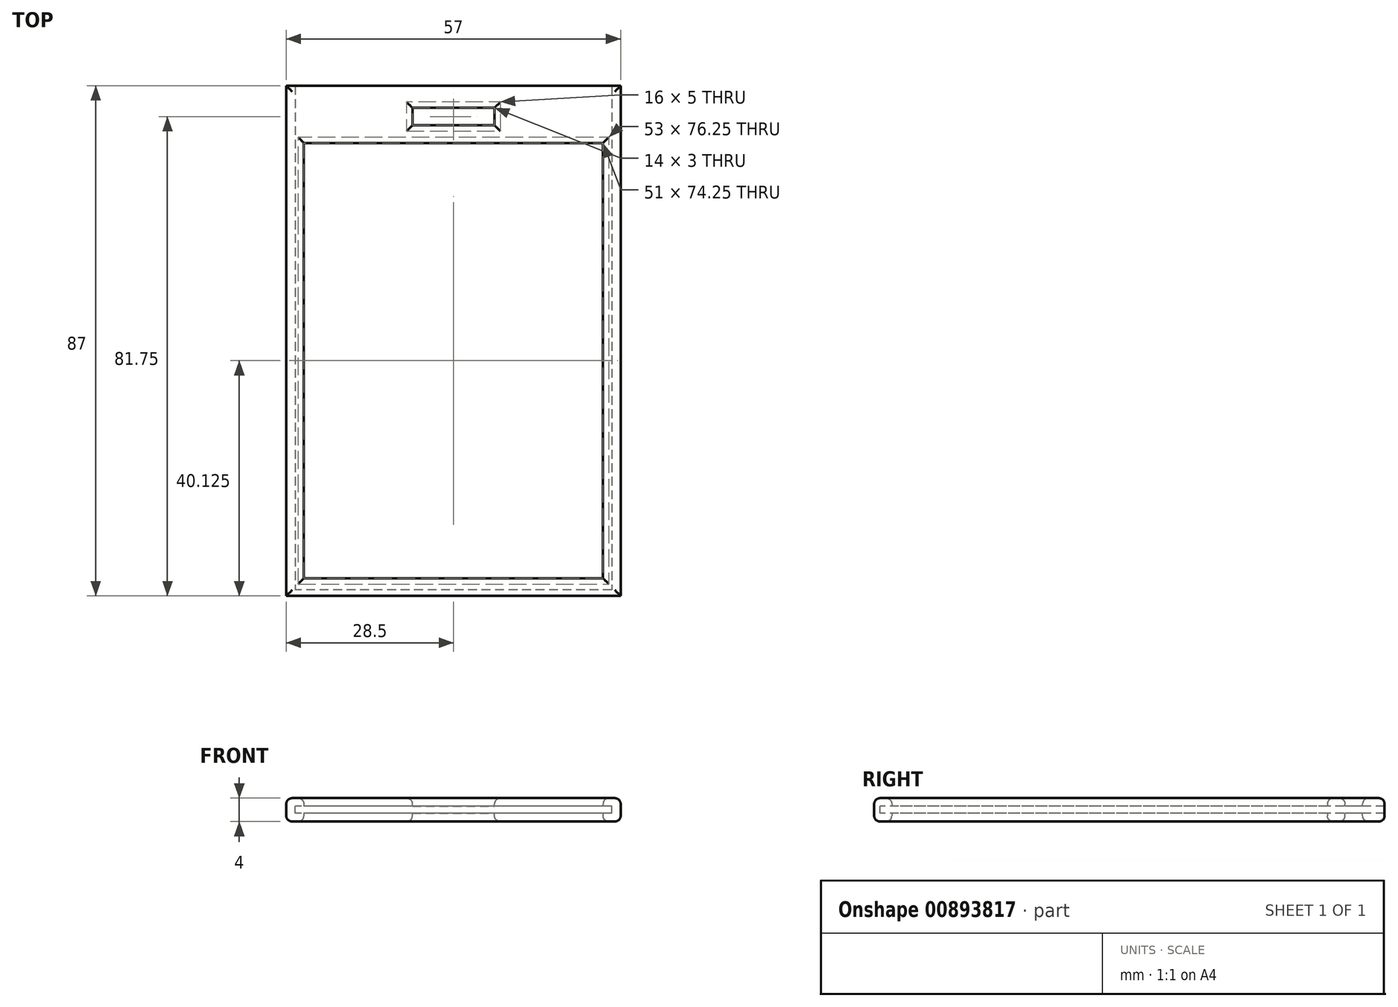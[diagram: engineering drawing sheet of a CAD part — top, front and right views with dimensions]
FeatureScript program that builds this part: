
annotation { "Feature Type Name" : "Feature", "Feature Type Description" : "" }
export const myFeature = defineFeature(function(context is Context, id is Id, definition is map)
    precondition{}
    {
        {
            var Q0;
            Q0=qCreatedBy(makeId("Top.planeOp"),FACE);
            var sketch = newSketch(context, id + "F0", { "sketchPlane" : qUnion([Q0])});
            skLineSegment(sketch, "E0.bottom", {"start": v(28.5, -43.5) * mm, "end": v(-28.5, -43.5) * mm});
            skLineSegment(sketch, "E0.top", {"start": v(28.5, 43.5) * mm, "end": v(-28.5, 43.5) * mm});
            skLineSegment(sketch, "E0.left", {"start": v(28.5, -43.5) * mm, "end": v(28.5, 43.5) * mm});
            skLineSegment(sketch, "E0.right", {"start": v(-28.5, -43.5) * mm, "end": v(-28.5, 43.5) * mm});
            skPoint(sketch, "E0.middle", {"position": v(0, 0) * mm});
            skSolve(sketch);
        }
        {
            var Q0;
            Q0 = qSketchRegion(id + "F0", true);
            extrude(context, id + "F1", {"entities" : qUnion([Q0]), "endBound" : BoundingType.SYMMETRIC, "depth" : 4 * mm, "offsetDistance" : 25 * mm});
        }
        {
            var Q0;
            Q0=qCreatedBy(makeId("Top.planeOp"),FACE);
            var sketch = newSketch(context, id + "F2", { "sketchPlane" : qUnion([Q0])});
            skLineSegment(sketch, "E1.bottom", {"start": v(7, 36.75) * mm, "end": v(-7, 36.75) * mm});
            skLineSegment(sketch, "E1.top", {"start": v(7, 39.75) * mm, "end": v(-7, 39.75) * mm});
            skLineSegment(sketch, "E1.left", {"start": v(7, 36.75) * mm, "end": v(7, 39.75) * mm});
            skLineSegment(sketch, "E1.right", {"start": v(-7, 36.75) * mm, "end": v(-7, 39.75) * mm});
            skPoint(sketch, "E1.middle", {"position": v(0, 38.25) * mm});
            skSolve(sketch);
        }
        {
            var Q0;
            Q0 = qSketchRegion(id + "F2", true);
            extrude(context, id + "F3", {"entities" : qUnion([Q0]), "operationType" : NewBodyOperationType.REMOVE, "endBound" : BoundingType.SYMMETRIC, "oppositeDirection" : true, "depth" : 25 * mm, "offsetDistance" : 25 * mm});
        }
        {
            var Q0;
            Q0=qCreatedBy(makeId("Front.planeOp"),FACE);
            var sketch = newSketch(context, id + "F4", { "sketchPlane" : qUnion([Q0])});
            skLineSegment(sketch, "E2.bottom", {"start": v(27, -0.6) * mm, "end": v(-27, -0.6) * mm});
            skLineSegment(sketch, "E2.top", {"start": v(27, 0.6) * mm, "end": v(-27, 0.6) * mm});
            skLineSegment(sketch, "E2.left", {"start": v(27, -0.6) * mm, "end": v(27, 0.6) * mm});
            skLineSegment(sketch, "E2.right", {"start": v(-27, -0.6) * mm, "end": v(-27, 0.6) * mm});
            skPoint(sketch, "E2.middle", {"position": v(0, 0) * mm});
            skSolve(sketch);
        }
        {
            var Q0;
            Q0 = qSketchRegion(id + "F4", true);
            extrude(context, id + "F5", {"entities" : qUnion([Q0]), "operationType" : NewBodyOperationType.REMOVE, "oppositeDirection" : true, "depth" : 50 * mm, "offsetDistance" : 25 * mm, "hasSecondDirection" : true, "secondDirectionOppositeDirection" : false, "secondDirectionDepth" : 42.5 * mm});
        }
        {
            var Q0;
            Q0=qCreatedBy(makeId("Top.planeOp"),FACE);
            var sketch = newSketch(context, id + "F6", { "sketchPlane" : qUnion([Q0])});
            skLineSegment(sketch, "E3.bottom", {"start": v(0, 0) * mm, "end": v(25.5, 0) * mm});
            skLineSegment(sketch, "E3.top", {"start": v(0, 33.75) * mm, "end": v(25.5, 33.75) * mm});
            skLineSegment(sketch, "E3.left", {"start": v(0, 0) * mm, "end": v(0, 33.75) * mm});
            skLineSegment(sketch, "E3.right", {"start": v(25.5, 0) * mm, "end": v(25.5, 33.75) * mm});
            skLineSegment(sketch, "E4.top", {"start": v(0, -40.5) * mm, "end": v(25.5, -40.5) * mm});
            skLineSegment(sketch, "E4.left", {"start": v(0, 0) * mm, "end": v(0, -40.5) * mm});
            skLineSegment(sketch, "E4.right", {"start": v(25.5, 0) * mm, "end": v(25.5, -40.5) * mm});
            skLineSegment(sketch, "E5.bottom", {"start": v(0, 0) * mm, "end": v(-25.5, 0) * mm});
            skLineSegment(sketch, "E5.top", {"start": v(0, -40.5) * mm, "end": v(-25.5, -40.5) * mm});
            skLineSegment(sketch, "E5.right", {"start": v(-25.5, 0) * mm, "end": v(-25.5, -40.5) * mm});
            skLineSegment(sketch, "E6.top", {"start": v(0, 33.75) * mm, "end": v(-25.5, 33.75) * mm});
            skLineSegment(sketch, "E6.right", {"start": v(-25.5, 0) * mm, "end": v(-25.5, 33.75) * mm});
            skSolve(sketch);
        }
        {
            var Q0;
            Q0 = qSketchRegion(id + "F6", true);
            extrude(context, id + "F7", {"entities" : qUnion([Q0]), "operationType" : NewBodyOperationType.REMOVE, "endBound" : BoundingType.SYMMETRIC, "depth" : 25 * mm, "offsetDistance" : 25 * mm});
        }
        {
            var Q0;
            Q0=makeQuery(id+"F1.opExtrude","CAP_EDGE",EDGE,{"disambiguationData":[OSD([sQuery(id+"F0.wireOp",EDGE,"E0.right")])],"isStart":false});
            var Q1;
            Q1=makeQuery(id+"F7.boolean.opBoolean","INTERSECT",EDGE,{"derivedFrom":[makeQuery(id+"F1.opExtrude","CAP_FACE",FACE,{"disambiguationData":[OSD([sQuery(id+"F0.wireOp",EDGE,"E0.bottom"),sQuery(id+"F0.wireOp",EDGE,"E0.top"),sQuery(id+"F0.wireOp",EDGE,"E0.left"),sQuery(id+"F0.wireOp",EDGE,"E0.right")])],"isStart":false}),makeQuery(id+"F7.opExtrude","SWEPT_FACE",FACE,{"disambiguationData":[OSD([sQuery(id+"F6.wireOp",EDGE,"E5.right"),sQuery(id+"F6.wireOp",EDGE,"E6.right")])]})]});
            var Q2;
            Q2=makeQuery(id+"F7.boolean.opBoolean","INTERSECT",EDGE,{"derivedFrom":[makeQuery(id+"F1.opExtrude","CAP_FACE",FACE,{"disambiguationData":[OSD([sQuery(id+"F0.wireOp",EDGE,"E0.bottom"),sQuery(id+"F0.wireOp",EDGE,"E0.top"),sQuery(id+"F0.wireOp",EDGE,"E0.left"),sQuery(id+"F0.wireOp",EDGE,"E0.right")])],"isStart":false}),makeQuery(id+"F7.opExtrude","SWEPT_FACE",FACE,{"disambiguationData":[OSD([sQuery(id+"F6.wireOp",EDGE,"E4.top"),sQuery(id+"F6.wireOp",EDGE,"E5.top")])]})]});
            var Q3;
            Q3=makeQuery(id+"F1.opExtrude","CAP_EDGE",EDGE,{"disambiguationData":[OSD([sQuery(id+"F0.wireOp",EDGE,"E0.bottom")])],"isStart":false});
            var Q4;
            Q4=makeQuery(id+"F7.boolean.opBoolean","INTERSECT",EDGE,{"derivedFrom":[makeQuery(id+"F1.opExtrude","CAP_FACE",FACE,{"disambiguationData":[OSD([sQuery(id+"F0.wireOp",EDGE,"E0.bottom"),sQuery(id+"F0.wireOp",EDGE,"E0.top"),sQuery(id+"F0.wireOp",EDGE,"E0.left"),sQuery(id+"F0.wireOp",EDGE,"E0.right")])],"isStart":false}),makeQuery(id+"F7.opExtrude","SWEPT_FACE",FACE,{"disambiguationData":[OSD([sQuery(id+"F6.wireOp",EDGE,"E3.right"),sQuery(id+"F6.wireOp",EDGE,"E4.right")])]})]});
            var Q5;
            Q5=makeQuery(id+"F1.opExtrude","CAP_EDGE",EDGE,{"disambiguationData":[OSD([sQuery(id+"F0.wireOp",EDGE,"E0.left")])],"isStart":false});
            var Q6;
            Q6=makeQuery(id+"F7.boolean.opBoolean","INTERSECT",EDGE,{"derivedFrom":[makeQuery(id+"F1.opExtrude","CAP_FACE",FACE,{"disambiguationData":[OSD([sQuery(id+"F0.wireOp",EDGE,"E0.bottom"),sQuery(id+"F0.wireOp",EDGE,"E0.top"),sQuery(id+"F0.wireOp",EDGE,"E0.left"),sQuery(id+"F0.wireOp",EDGE,"E0.right")])],"isStart":false}),makeQuery(id+"F7.opExtrude","SWEPT_FACE",FACE,{"disambiguationData":[OSD([sQuery(id+"F6.wireOp",EDGE,"E3.top"),sQuery(id+"F6.wireOp",EDGE,"E6.top")])]})]});
            var Q7;
            Q7=makeQuery(id+"F1.opExtrude","CAP_EDGE",EDGE,{"disambiguationData":[OSD([sQuery(id+"F0.wireOp",EDGE,"E0.top")])],"isStart":false});
            var Q8;
            Q8=makeQuery(id+"F1.opExtrude","CAP_EDGE",EDGE,{"disambiguationData":[OSD([sQuery(id+"F0.wireOp",EDGE,"E0.right")])],"isStart":true});
            var Q9;
            Q9=makeQuery(id+"F1.opExtrude","CAP_EDGE",EDGE,{"disambiguationData":[OSD([sQuery(id+"F0.wireOp",EDGE,"E0.top")])],"isStart":true});
            var Q10;
            Q10=makeQuery(id+"F7.boolean.opBoolean","INTERSECT",EDGE,{"derivedFrom":[makeQuery(id+"F1.opExtrude","CAP_FACE",FACE,{"disambiguationData":[OSD([sQuery(id+"F0.wireOp",EDGE,"E0.bottom"),sQuery(id+"F0.wireOp",EDGE,"E0.top"),sQuery(id+"F0.wireOp",EDGE,"E0.left"),sQuery(id+"F0.wireOp",EDGE,"E0.right")])],"isStart":true}),makeQuery(id+"F7.opExtrude","SWEPT_FACE",FACE,{"disambiguationData":[OSD([sQuery(id+"F6.wireOp",EDGE,"E3.top"),sQuery(id+"F6.wireOp",EDGE,"E6.top")])]})]});
            var Q11;
            Q11=makeQuery(id+"F7.boolean.opBoolean","INTERSECT",EDGE,{"derivedFrom":[makeQuery(id+"F1.opExtrude","CAP_FACE",FACE,{"disambiguationData":[OSD([sQuery(id+"F0.wireOp",EDGE,"E0.bottom"),sQuery(id+"F0.wireOp",EDGE,"E0.top"),sQuery(id+"F0.wireOp",EDGE,"E0.left"),sQuery(id+"F0.wireOp",EDGE,"E0.right")])],"isStart":true}),makeQuery(id+"F7.opExtrude","SWEPT_FACE",FACE,{"disambiguationData":[OSD([sQuery(id+"F6.wireOp",EDGE,"E3.right"),sQuery(id+"F6.wireOp",EDGE,"E4.right")])]})]});
            var Q12;
            Q12=makeQuery(id+"F7.boolean.opBoolean","INTERSECT",EDGE,{"derivedFrom":[makeQuery(id+"F1.opExtrude","CAP_FACE",FACE,{"disambiguationData":[OSD([sQuery(id+"F0.wireOp",EDGE,"E0.bottom"),sQuery(id+"F0.wireOp",EDGE,"E0.top"),sQuery(id+"F0.wireOp",EDGE,"E0.left"),sQuery(id+"F0.wireOp",EDGE,"E0.right")])],"isStart":true}),makeQuery(id+"F7.opExtrude","SWEPT_FACE",FACE,{"disambiguationData":[OSD([sQuery(id+"F6.wireOp",EDGE,"E5.right"),sQuery(id+"F6.wireOp",EDGE,"E6.right")])]})]});
            var Q13;
            Q13=makeQuery(id+"F1.opExtrude","CAP_EDGE",EDGE,{"disambiguationData":[OSD([sQuery(id+"F0.wireOp",EDGE,"E0.left")])],"isStart":true});
            var Q14;
            Q14=makeQuery(id+"F7.boolean.opBoolean","INTERSECT",EDGE,{"derivedFrom":[makeQuery(id+"F1.opExtrude","CAP_FACE",FACE,{"disambiguationData":[OSD([sQuery(id+"F0.wireOp",EDGE,"E0.bottom"),sQuery(id+"F0.wireOp",EDGE,"E0.top"),sQuery(id+"F0.wireOp",EDGE,"E0.left"),sQuery(id+"F0.wireOp",EDGE,"E0.right")])],"isStart":true}),makeQuery(id+"F7.opExtrude","SWEPT_FACE",FACE,{"disambiguationData":[OSD([sQuery(id+"F6.wireOp",EDGE,"E4.top"),sQuery(id+"F6.wireOp",EDGE,"E5.top")])]})]});
            var Q15;
            Q15=makeQuery(id+"F3.boolean.opBoolean","INTERSECT",EDGE,{"derivedFrom":[makeQuery(id+"F1.opExtrude","CAP_FACE",FACE,{"disambiguationData":[OSD([sQuery(id+"F0.wireOp",EDGE,"E0.bottom"),sQuery(id+"F0.wireOp",EDGE,"E0.top"),sQuery(id+"F0.wireOp",EDGE,"E0.left"),sQuery(id+"F0.wireOp",EDGE,"E0.right")])],"isStart":true}),makeQuery(id+"F3.opExtrude","SWEPT_FACE",FACE,{"disambiguationData":[OSD([sQuery(id+"F2.wireOp",EDGE,"E1.bottom")])]})]});
            var Q16;
            Q16=makeQuery(id+"F3.boolean.opBoolean","INTERSECT",EDGE,{"derivedFrom":[makeQuery(id+"F1.opExtrude","CAP_FACE",FACE,{"disambiguationData":[OSD([sQuery(id+"F0.wireOp",EDGE,"E0.bottom"),sQuery(id+"F0.wireOp",EDGE,"E0.top"),sQuery(id+"F0.wireOp",EDGE,"E0.left"),sQuery(id+"F0.wireOp",EDGE,"E0.right")])],"isStart":true}),makeQuery(id+"F3.opExtrude","SWEPT_FACE",FACE,{"disambiguationData":[OSD([sQuery(id+"F2.wireOp",EDGE,"E1.left")])]})]});
            var Q17;
            Q17=makeQuery(id+"F3.boolean.opBoolean","INTERSECT",EDGE,{"derivedFrom":[makeQuery(id+"F1.opExtrude","CAP_FACE",FACE,{"disambiguationData":[OSD([sQuery(id+"F0.wireOp",EDGE,"E0.bottom"),sQuery(id+"F0.wireOp",EDGE,"E0.top"),sQuery(id+"F0.wireOp",EDGE,"E0.left"),sQuery(id+"F0.wireOp",EDGE,"E0.right")])],"isStart":true}),makeQuery(id+"F3.opExtrude","SWEPT_FACE",FACE,{"disambiguationData":[OSD([sQuery(id+"F2.wireOp",EDGE,"E1.right")])]})]});
            var Q18;
            Q18=makeQuery(id+"F3.boolean.opBoolean","INTERSECT",EDGE,{"derivedFrom":[makeQuery(id+"F1.opExtrude","CAP_FACE",FACE,{"disambiguationData":[OSD([sQuery(id+"F0.wireOp",EDGE,"E0.bottom"),sQuery(id+"F0.wireOp",EDGE,"E0.top"),sQuery(id+"F0.wireOp",EDGE,"E0.left"),sQuery(id+"F0.wireOp",EDGE,"E0.right")])],"isStart":true}),makeQuery(id+"F3.opExtrude","SWEPT_FACE",FACE,{"disambiguationData":[OSD([sQuery(id+"F2.wireOp",EDGE,"E1.top")])]})]});
            var Q19;
            Q19=makeQuery(id+"F3.boolean.opBoolean","INTERSECT",EDGE,{"derivedFrom":[makeQuery(id+"F1.opExtrude","CAP_FACE",FACE,{"disambiguationData":[OSD([sQuery(id+"F0.wireOp",EDGE,"E0.bottom"),sQuery(id+"F0.wireOp",EDGE,"E0.top"),sQuery(id+"F0.wireOp",EDGE,"E0.left"),sQuery(id+"F0.wireOp",EDGE,"E0.right")])],"isStart":false}),makeQuery(id+"F3.opExtrude","SWEPT_FACE",FACE,{"disambiguationData":[OSD([sQuery(id+"F2.wireOp",EDGE,"E1.bottom")])]})]});
            var Q20;
            Q20=makeQuery(id+"F3.boolean.opBoolean","INTERSECT",EDGE,{"derivedFrom":[makeQuery(id+"F1.opExtrude","CAP_FACE",FACE,{"disambiguationData":[OSD([sQuery(id+"F0.wireOp",EDGE,"E0.bottom"),sQuery(id+"F0.wireOp",EDGE,"E0.top"),sQuery(id+"F0.wireOp",EDGE,"E0.left"),sQuery(id+"F0.wireOp",EDGE,"E0.right")])],"isStart":false}),makeQuery(id+"F3.opExtrude","SWEPT_FACE",FACE,{"disambiguationData":[OSD([sQuery(id+"F2.wireOp",EDGE,"E1.right")])]})]});
            var Q21;
            Q21=makeQuery(id+"F3.boolean.opBoolean","INTERSECT",EDGE,{"derivedFrom":[makeQuery(id+"F1.opExtrude","CAP_FACE",FACE,{"disambiguationData":[OSD([sQuery(id+"F0.wireOp",EDGE,"E0.bottom"),sQuery(id+"F0.wireOp",EDGE,"E0.top"),sQuery(id+"F0.wireOp",EDGE,"E0.left"),sQuery(id+"F0.wireOp",EDGE,"E0.right")])],"isStart":false}),makeQuery(id+"F3.opExtrude","SWEPT_FACE",FACE,{"disambiguationData":[OSD([sQuery(id+"F2.wireOp",EDGE,"E1.left")])]})]});
            var Q22;
            Q22=makeQuery(id+"F1.opExtrude","CAP_EDGE",EDGE,{"disambiguationData":[OSD([sQuery(id+"F0.wireOp",EDGE,"E0.bottom")])],"isStart":true});
            var Q23;
            Q23=makeQuery(id+"F3.boolean.opBoolean","INTERSECT",EDGE,{"derivedFrom":[makeQuery(id+"F1.opExtrude","CAP_FACE",FACE,{"disambiguationData":[OSD([sQuery(id+"F0.wireOp",EDGE,"E0.bottom"),sQuery(id+"F0.wireOp",EDGE,"E0.top"),sQuery(id+"F0.wireOp",EDGE,"E0.left"),sQuery(id+"F0.wireOp",EDGE,"E0.right")])],"isStart":false}),makeQuery(id+"F3.opExtrude","SWEPT_FACE",FACE,{"disambiguationData":[OSD([sQuery(id+"F2.wireOp",EDGE,"E1.top")])]})]});
            fillet(context, id + "F8", {"entities" : qUnion([Q0, Q1, Q2, Q3, Q4, Q5, Q6, Q7, Q8, Q9, Q10, Q11, Q12, Q13, Q14, Q15, Q16, Q17, Q18, Q19, Q20, Q21, Q22, Q23]), "radius" : 1 * mm, "tangentPropagation" : true, "allowEdgeOverflow" : false});
        }
    });
